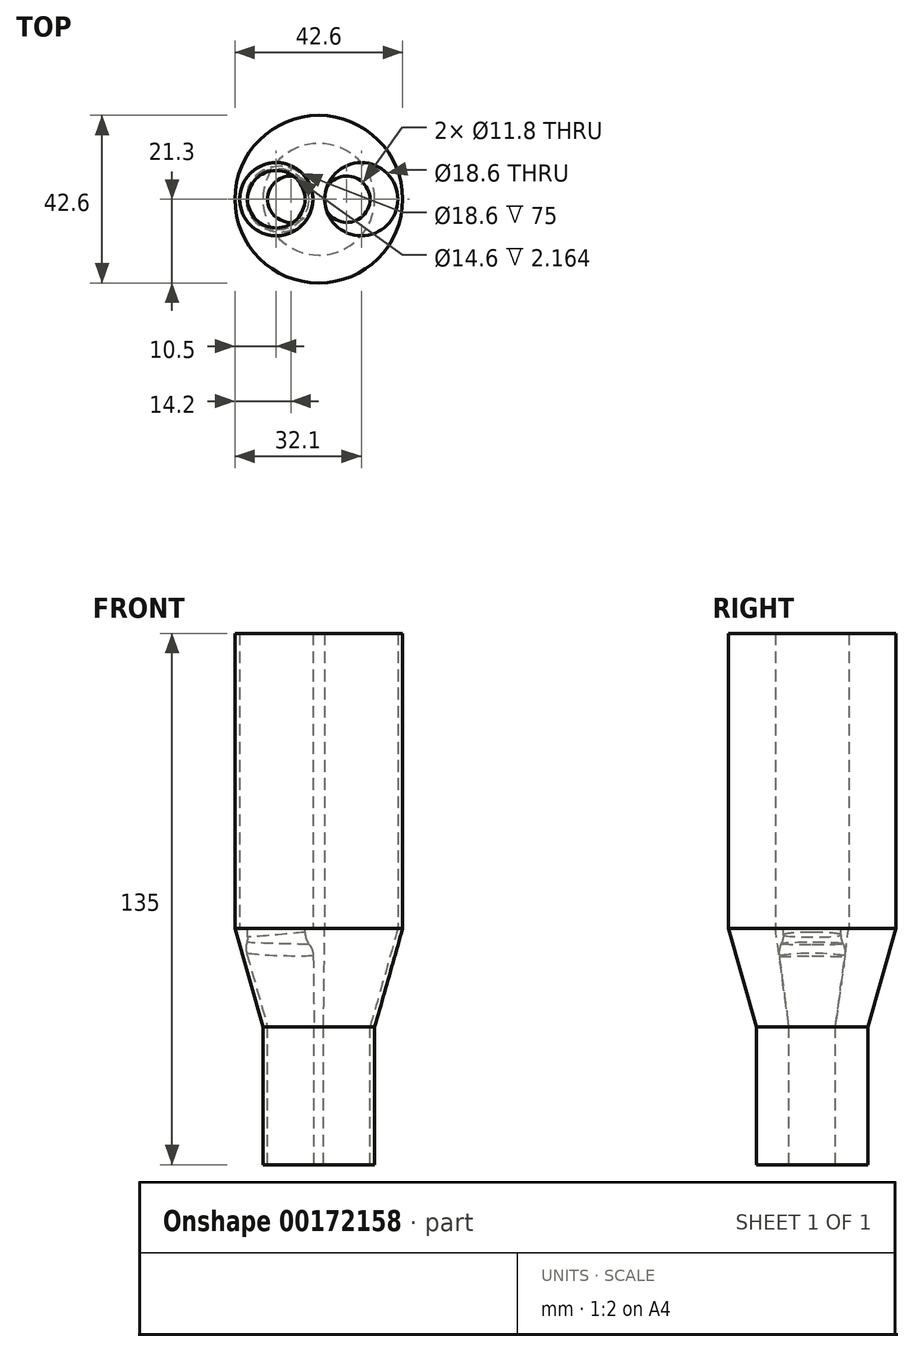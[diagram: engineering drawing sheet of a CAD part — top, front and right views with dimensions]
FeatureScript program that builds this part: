
annotation { "Feature Type Name" : "Feature", "Feature Type Description" : "" }
export const myFeature = defineFeature(function(context is Context, id is Id, definition is map)
    precondition{}
    {
        {
            var Q0;
            Q0=qCreatedBy(makeId("Top.planeOp"),FACE);
            var sketch = newSketch(context, id + "F0", { "sketchPlane" : qUnion([Q0])});
            skCircle(sketch, "E0", {"center": v(0, 0) * mm, "radius": 14.5 * mm, "construction": true});
            skCircle(sketch, "E1", {"center": v(-10.8, 0) * mm, "radius": 9 * mm, "construction": true});
            skCircle(sketch, "E2", {"center": v(-10.8, 0) * mm, "radius": 9.3 * mm});
            skLineSegment(sketch, "E3", {"start": v(-1.5, 0) * mm, "end": v(-1.5, 7.89) * mm, "construction": true});
            skLineSegment(sketch, "E4", {"start": v(0, 25.77) * mm, "end": v(0, -33.6) * mm, "construction": true});
            skCircle(sketch, "E5.MirrorC", {"center": v(10.8, 0) * mm, "radius": 9.3 * mm});
            skCircle(sketch, "E6", {"center": v(0, 0) * mm, "radius": 21.3 * mm});
            skLineSegment(sketch, "E7", {"start": v(-21.3, 0) * mm, "end": v(-21.3, -22.8) * mm, "construction": true});
            skLineSegment(sketch, "E8", {"start": v(-20.1, 0) * mm, "end": v(-20.1, -22.16) * mm, "construction": true});
            skSolve(sketch);
        }
        {
            var Q0;
            Q0=makeQuery(id+"F0.imprint","IMPRINT",FACE,{"disambiguationData":[TD([[makeQuery(id+"F0.imprint","IMPRINT",EDGE,{"derivedFrom":sQuery(id+"F0.wireOp",EDGE,"E2")}),-1.0]])]});
            extrude(context, id + "F1", {"entities" : qUnion([Q0]), "depth" : 75 * mm});
        }
        {
            var Q0;
            Q0=makeQuery(id+"F1.opExtrude","CAP_FACE",FACE,{"disambiguationData":[OSD([sQuery(id+"F0.wireOp",EDGE,"E2"),sQuery(id+"F0.wireOp",EDGE,"E5.MirrorC"),sQuery(id+"F0.wireOp",EDGE,"E6")])],"isStart":true});
            var sketch = newSketch(context, id + "F2", { "sketchPlane" : qUnion([Q0])});
            skCircle(sketch, "E9", {"center": v(0, 0) * mm, "radius": 21.3 * mm});
            skCircle(sketch, "E10", {"center": v(-10.8, 0) * mm, "radius": 9.3 * mm});
            skCircle(sketch, "E11", {"center": v(10.8, 0) * mm, "radius": 9.3 * mm});
            skSolve(sketch);
        }
        {
            var Q0;
            Q0=qCreatedBy(makeId("Top.planeOp"),FACE);
            cPlane(context, id + "F3", {"entities" : qUnion([Q0]), "cplaneType" : CPlaneType.OFFSET, "offset" : 25 * mm, "oppositeDirection" : true, "width" : 150 * mm, "height" : 150 * mm});
        }
        {
            var Q0;
            Q0=qCreatedBy(id+"F3.planeOp",FACE);
            var sketch = newSketch(context, id + "F4", { "sketchPlane" : qUnion([Q0])});
            skCircle(sketch, "E12", {"center": v(0, 0) * mm, "radius": 14.5 * mm, "construction": true});
            skCircle(sketch, "E13", {"center": v(0, 0) * mm, "radius": 14.2 * mm});
            skCircle(sketch, "E14", {"center": v(7.1, 0) * mm, "radius": 5.9 * mm});
            skLineSegment(sketch, "E15", {"start": v(0, 0) * mm, "end": v(14.2, 0) * mm});
            skLineSegment(sketch, "E16", {"start": v(13, 0) * mm, "end": v(13, 4.82) * mm, "construction": true});
            skLineSegment(sketch, "E17", {"start": v(14.2, 0) * mm, "end": v(14.2, 6.94) * mm, "construction": true});
            skLineSegment(sketch, "E18", {"start": v(0, -10.34) * mm, "end": v(0, 17.07) * mm, "construction": true});
            skCircle(sketch, "E19.MirrorC", {"center": v(-7.1, 0) * mm, "radius": 5.9 * mm});
            skSolve(sketch);
        }
        {
            var Q0;
            Q0=makeQuery(id+"F2.imprint","IMPRINT",FACE,{"disambiguationData":[TD([[makeQuery(id+"F2.imprint","IMPRINT",EDGE,{"derivedFrom":sQuery(id+"F2.wireOp",EDGE,"E9")}),-1.0]])]});
            var sketch = newSketch(context, id + "F5", { "sketchPlane" : qUnion([Q0])});
            skCircle(sketch, "E20", {"center": v(0, 0) * mm, "radius": 21.3 * mm});
            skSolve(sketch);
        }
        {
            var Q0;
            Q0=makeQuery(id+"F4.imprint","IMPRINT",FACE,{"disambiguationData":[TD([[makeQuery(id+"F4.imprint","IMPRINT",EDGE,{"derivedFrom":sQuery(id+"F4.wireOp",EDGE,"E13")}),1.0]])]});
            var sketch = newSketch(context, id + "F6", { "sketchPlane" : qUnion([Q0])});
            skCircle(sketch, "E21", {"center": v(0, 0) * mm, "radius": 14.2 * mm});
            skSolve(sketch);
        }
        {
            var Q1;
            Q1 = qSketchRegion(id + "F5", true);
            var Q2;
            Q2 = qSketchRegion(id + "F6", true);
            loft(context, id + "F7", {"operationType" : NewBodyOperationType.ADD, "sheetProfilesArray" : [{ "sheetProfileEntities" : qUnion([Q1]) }, { "sheetProfileEntities" : qUnion([Q2]) }]});
        }
        {
            var Q0;
            Q0=qCreatedBy(makeId("Top.planeOp"),FACE);
            var sketch = newSketch(context, id + "F8", { "sketchPlane" : qUnion([Q0])});
            skCircle(sketch, "E22", {"center": v(-10.8, 0) * mm, "radius": 9.3 * mm});
            skSolve(sketch);
        }
        {
            var Q0;
            Q0=makeQuery(id+"F4.imprint","IMPRINT",FACE,{"disambiguationData":[TD([[makeQuery(id+"F4.imprint","IMPRINT",EDGE,{"derivedFrom":sQuery(id+"F4.wireOp",EDGE,"E13")}),1.0]])]});
            var sketch = newSketch(context, id + "F9", { "sketchPlane" : qUnion([Q0])});
            skCircle(sketch, "E23", {"center": v(-7.1, 0) * mm, "radius": 5.9 * mm});
            skSolve(sketch);
        }
        {
            var Q1;
            Q1 = qSketchRegion(id + "F8", true);
            var Q2;
            Q2 = qSketchRegion(id + "F9", true);
            loft(context, id + "F10", {"operationType" : NewBodyOperationType.REMOVE, "sheetProfilesArray" : [{ "sheetProfileEntities" : qUnion([Q1]) }, { "sheetProfileEntities" : qUnion([Q2]) }]});
        }
        {
            var Q0;
            Q0=qCreatedBy(makeId("Top.planeOp"),FACE);
            var sketch = newSketch(context, id + "F11", { "sketchPlane" : qUnion([Q0])});
            skCircle(sketch, "E24", {"center": v(10.8, 0) * mm, "radius": 9.3 * mm});
            skSolve(sketch);
        }
        {
            var Q0;
            Q0=makeQuery(id+"F4.imprint","IMPRINT",FACE,{"disambiguationData":[TD([[makeQuery(id+"F4.imprint","IMPRINT",EDGE,{"derivedFrom":sQuery(id+"F4.wireOp",EDGE,"E13")}),1.0]])]});
            var sketch = newSketch(context, id + "F12", { "sketchPlane" : qUnion([Q0])});
            skCircle(sketch, "E25", {"center": v(7.1, 0) * mm, "radius": 5.9 * mm});
            skSolve(sketch);
        }
        {
            var Q1;
            Q1 = qSketchRegion(id + "F11", true);
            var Q2;
            Q2 = qSketchRegion(id + "F12", true);
            loft(context, id + "F13", {"operationType" : NewBodyOperationType.REMOVE, "sheetProfilesArray" : [{ "sheetProfileEntities" : qUnion([Q1]) }, { "sheetProfileEntities" : qUnion([Q2]) }]});
        }
        {
            var Q0;
            Q0=makeQuery(id+"F4.imprint","IMPRINT",FACE,{"disambiguationData":[TD([[makeQuery(id+"F4.imprint","IMPRINT",EDGE,{"derivedFrom":sQuery(id+"F4.wireOp",EDGE,"E13")}),1.0]])]});
            var sketch = newSketch(context, id + "F14", { "sketchPlane" : qUnion([Q0])});
            skCircle(sketch, "E26", {"center": v(0, 0) * mm, "radius": 14.2 * mm});
            skCircle(sketch, "E27", {"center": v(7.1, 0) * mm, "radius": 5.9 * mm});
            skCircle(sketch, "E28", {"center": v(-7.1, 0) * mm, "radius": 5.9 * mm});
            skSolve(sketch);
        }
        {
            var Q0;
            Q0 = qSketchRegion(id + "F14", true);
            extrude(context, id + "F15", {"entities" : qUnion([Q0]), "operationType" : NewBodyOperationType.ADD, "oppositeDirection" : true, "depth" : 35 * mm});
        }
        {
            var Q0;
            Q0=qCreatedBy(makeId("Top.planeOp"),FACE);
            var sketch = newSketch(context, id + "F16", { "sketchPlane" : qUnion([Q0])});
            skCircle(sketch, "E29", {"center": v(-10.8, 0) * mm, "radius": 7.3 * mm});
            skCircle(sketch, "E30", {"center": v(-10.8, 0) * mm, "radius": 9.4 * mm});
            skSolve(sketch);
        }
        {
            var Q0;
            Q0 = qSketchRegion(id + "F16", true);
            extrude(context, id + "F17", {"entities" : qUnion([Q0]), "operationType" : NewBodyOperationType.ADD, "oppositeDirection" : true, "depth" : 3 * mm});
        }
        {
            var Q0;
            Q0=makeQuery(id+"F17.boolean.opBoolean","INTERSECT",EDGE,{"derivedFrom":[makeQuery(id+"F10.boolean.opBoolean","COPY",FACE,{"derivedFrom":makeQuery(id+"F10.opLoft","SWEPT_FACE",FACE,{"disambiguationData":[OSD([sQuery(id+"F8.wireOp",EDGE,"E22"),sQuery(id+"F9.wireOp",EDGE,"E23")])]})}),makeQuery(id+"F17.opExtrude","CAP_FACE",FACE,{"disambiguationData":[OSD([sQuery(id+"F16.wireOp",EDGE,"E29"),sQuery(id+"F16.wireOp",EDGE,"E30")])],"isStart":false})]});
            fillet(context, id + "F18", {"entities" : qUnion([Q0]), "radius" : 5 * mm, "tangentPropagation" : true, "allowEdgeOverflow" : false});
        }
        {
            var Q0;
            {var subQ0=sQuery(id+"F16.wireOp",EDGE,"E29");Q0=makeQuery(id+"F18.opFillet","BLEND_EDGE",EDGE,{"blendedFrom":[makeQuery(id+"F17.boolean.opBoolean","INTERSECT",EDGE,{"derivedFrom":[makeQuery(id+"F10.boolean.opBoolean","COPY",FACE,{"derivedFrom":makeQuery(id+"F10.opLoft","SWEPT_FACE",FACE,{"disambiguationData":[OSD([sQuery(id+"F8.wireOp",EDGE,"E22"),sQuery(id+"F9.wireOp",EDGE,"E23")])]})}),makeQuery(id+"F17.opExtrude","CAP_FACE",FACE,{"disambiguationData":[OSD([subQ0,sQuery(id+"F16.wireOp",EDGE,"E30")])],"isStart":false})]}),makeQuery(id+"F17.opExtrude","SWEPT_FACE",FACE,{"disambiguationData":[OSD([subQ0])]})],"blendedInto":[makeQuery(id+"F17.opExtrude","SWEPT_FACE",FACE,{"disambiguationData":[OSD([subQ0])]})]});}
            fillet(context, id + "F19", {"entities" : qUnion([Q0]), "radius" : 5 * mm, "tangentPropagation" : true, "allowEdgeOverflow" : false});
        }
    });
